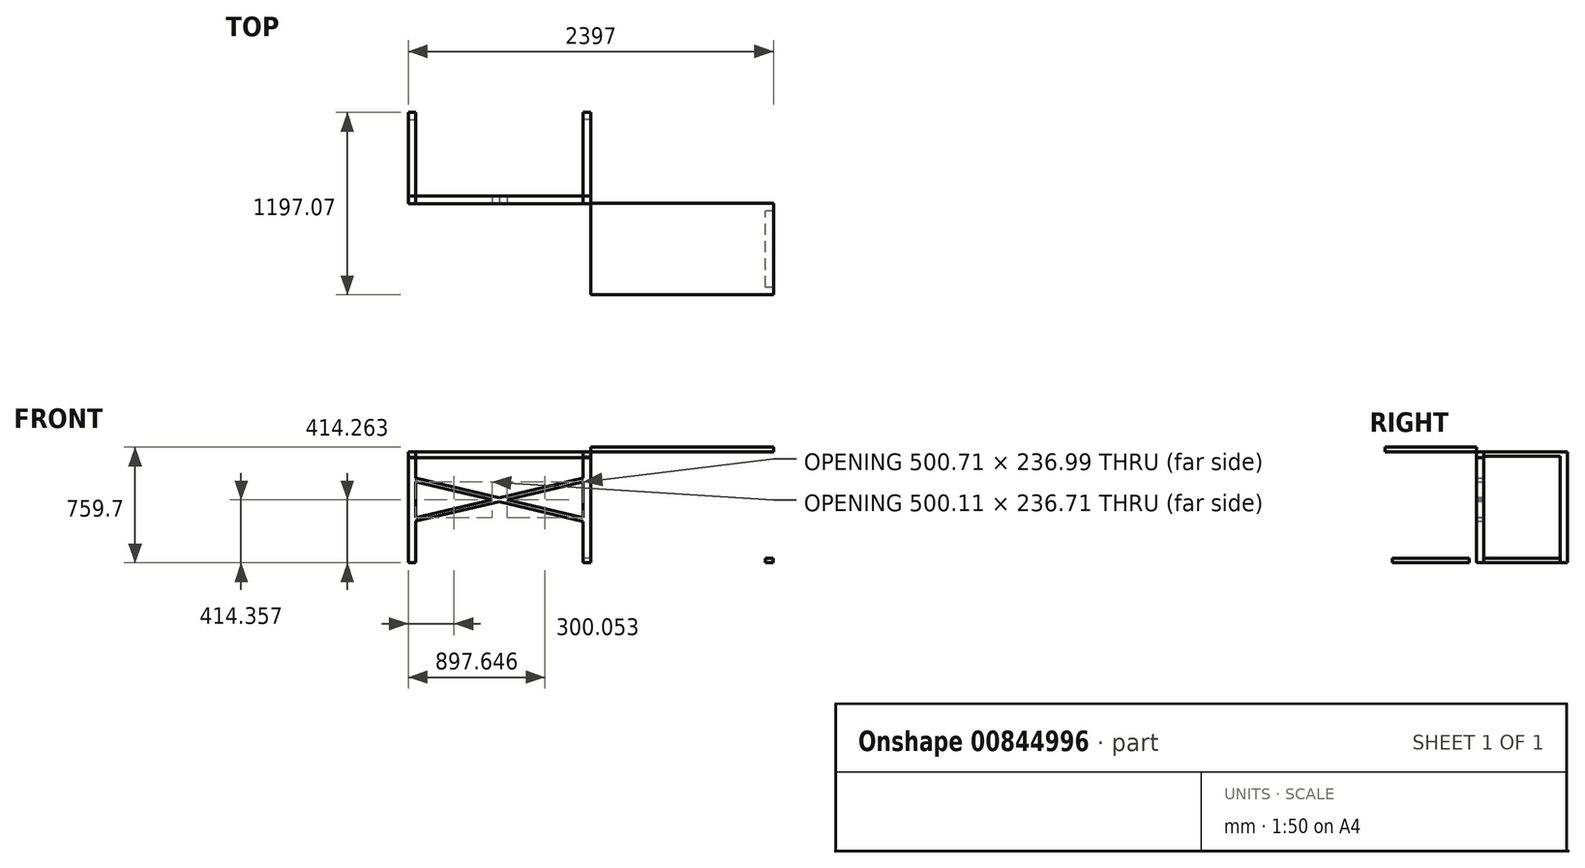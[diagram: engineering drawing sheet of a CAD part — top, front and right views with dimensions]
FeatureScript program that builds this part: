
annotation { "Feature Type Name" : "Feature", "Feature Type Description" : "" }
export const myFeature = defineFeature(function(context is Context, id is Id, definition is map)
    precondition{}
    {
        {
            var Q0;
            Q0=qCreatedBy(makeId("Top.planeOp"),FACE);
            var sketch = newSketch(context, id + "F0", { "sketchPlane" : qUnion([Q0])});
            skLineSegment(sketch, "E0.bottom", {"start": v(600, -300) * mm, "end": v(-600, -300) * mm});
            skLineSegment(sketch, "E0.top", {"start": v(600, 300) * mm, "end": v(-600, 300) * mm});
            skLineSegment(sketch, "E0.left", {"start": v(600, -300) * mm, "end": v(600, 300) * mm});
            skLineSegment(sketch, "E0.right", {"start": v(-600, -300) * mm, "end": v(-600, 300) * mm});
            skPoint(sketch, "E0.middle", {"position": v(0, 0) * mm});
            skSolve(sketch);
        }
        {
            var Q0;
            Q0 = qSketchRegion(id + "F0", true);
            extrude(context, id + "F1", {"entities" : qUnion([Q0]), "depth" : 30 * mm, "offsetDistance" : 25 * mm});
        }
        {
            var Q0;
            Q0=qCreatedBy(makeId("Right.planeOp"),FACE);
            var sketch = newSketch(context, id + "F2", { "sketchPlane" : qUnion([Q0])});
            skLineSegment(sketch, "E1.bottom", {"start": v(-299.02, 0) * mm, "end": v(299.02, 0) * mm});
            skLineSegment(sketch, "E1.top", {"start": v(-299.02, -29.7) * mm, "end": v(299.02, -29.7) * mm});
            skLineSegment(sketch, "E1.left", {"start": v(-299.02, 0) * mm, "end": v(-299.02, -29.7) * mm});
            skLineSegment(sketch, "E1.right", {"start": v(299.02, 0) * mm, "end": v(299.02, -29.7) * mm});
            skSolve(sketch);
        }
        {
            var Q0;
            Q0 = qSketchRegion(id + "F2", true);
            extrude(context, id + "F3", {"entities" : qUnion([Q0]), "depth" : 50 * mm, "offsetDistance" : 25 * mm});
        }
        {
            var Q0;
            Q0=makeQuery(id+"F3.opExtrude","SWEPT_BODY",BODY,{"disambiguationData":[OSD([sQuery(id+"F2.wireOp",EDGE,"E1.bottom"),sQuery(id+"F2.wireOp",EDGE,"E1.top"),sQuery(id+"F2.wireOp",EDGE,"E1.left"),sQuery(id+"F2.wireOp",EDGE,"E1.right")])]});
            transform(context, id + "F4", {"entities" : qUnion([Q0]), "transformType" : TransformType.TRANSLATION_3D, "dx" : 549 * mm, "dy" : 0 * mm, "dz" : 0 * mm, "makeCopy" : false});
        }
        {
            var Q0;
            Q0=makeQuery(id+"F3.opExtrude","SWEPT_BODY",BODY,{"disambiguationData":[OSD([sQuery(id+"F2.wireOp",EDGE,"E1.bottom"),sQuery(id+"F2.wireOp",EDGE,"E1.top"),sQuery(id+"F2.wireOp",EDGE,"E1.left"),sQuery(id+"F2.wireOp",EDGE,"E1.right")])]});
            var Q1;
            Q1=qCreatedBy(makeId("Right.planeOp"),FACE);
            mirror(context, id + "F5", {"entities" : qUnion([Q0]), "mirrorPlane" : qUnion([Q1])});
        }
        {
            var Q0;
            Q0=makeQuery(id+"F5.opPattern","COPY",FACE,{"derivedFrom":makeQuery(id+"F3.opExtrude","SWEPT_FACE",FACE,{"disambiguationData":[OSD([sQuery(id+"F2.wireOp",EDGE,"E1.top")])]}),"instanceName":"1"});
            var sketch = newSketch(context, id + "F6", { "sketchPlane" : qUnion([Q0])});
            skLineSegment(sketch, "E2.bottom", {"start": v(-599, -299.02) * mm, "end": v(-549, -299.02) * mm});
            skLineSegment(sketch, "E2.top", {"start": v(-599, -251.22) * mm, "end": v(-549, -251.22) * mm});
            skLineSegment(sketch, "E2.left", {"start": v(-599, -299.02) * mm, "end": v(-599, -251.22) * mm});
            skLineSegment(sketch, "E2.right", {"start": v(-549, -299.02) * mm, "end": v(-549, -251.22) * mm});
            skSolve(sketch);
        }
        {
            var Q0;
            Q0 = qSketchRegion(id + "F6", true);
            extrude(context, id + "F7", {"entities" : qUnion([Q0]), "depth" : 700 * mm, "offsetDistance" : 25 * mm});
        }
        {
            var Q0;
            Q0=makeQuery(id+"F7.opExtrude","SWEPT_BODY",BODY,{"disambiguationData":[OSD([sQuery(id+"F6.wireOp",EDGE,"E2.bottom"),sQuery(id+"F6.wireOp",EDGE,"E2.top"),sQuery(id+"F6.wireOp",EDGE,"E2.left"),sQuery(id+"F6.wireOp",EDGE,"E2.right")])]});
            var Q1;
            Q1=qCreatedBy(makeId("Right.planeOp"),FACE);
            mirror(context, id + "F8", {"entities" : qUnion([Q0]), "mirrorPlane" : qUnion([Q1])});
        }
        {
            var Q0;
            Q0=makeQuery(id+"F7.opExtrude","SWEPT_BODY",BODY,{"disambiguationData":[OSD([sQuery(id+"F6.wireOp",EDGE,"E2.bottom"),sQuery(id+"F6.wireOp",EDGE,"E2.top"),sQuery(id+"F6.wireOp",EDGE,"E2.left"),sQuery(id+"F6.wireOp",EDGE,"E2.right")])]});
            var Q1;
            Q1=qCreatedBy(makeId("Front.planeOp"),FACE);
            mirror(context, id + "F9", {"operationType" : NewBodyOperationType.ADD, "entities" : qUnion([Q0]), "mirrorPlane" : qUnion([Q1])});
        }
        {
            var Q0;
            Q0=makeQuery(id+"F8.opPattern","COPY",BODY,{"derivedFrom":makeQuery(id+"F7.opExtrude","SWEPT_BODY",BODY,{"disambiguationData":[OSD([sQuery(id+"F6.wireOp",EDGE,"E2.bottom"),sQuery(id+"F6.wireOp",EDGE,"E2.top"),sQuery(id+"F6.wireOp",EDGE,"E2.left"),sQuery(id+"F6.wireOp",EDGE,"E2.right")])]}),"instanceName":"1"});
            var Q1;
            Q1=qCreatedBy(makeId("Front.planeOp"),FACE);
            mirror(context, id + "F10", {"operationType" : NewBodyOperationType.ADD, "entities" : qUnion([Q0]), "mirrorPlane" : qUnion([Q1])});
        }
        {
            var Q0;
            Q0=qCreatedBy(makeId("Top.planeOp"),FACE);
            var sketch = newSketch(context, id + "F11", { "sketchPlane" : qUnion([Q0])});
            skLineSegment(sketch, "E3.bottom", {"start": v(-598.92, -299.03) * mm, "end": v(598.98, -299.03) * mm});
            skLineSegment(sketch, "E3.top", {"start": v(-598.92, -251.27) * mm, "end": v(598.98, -251.27) * mm});
            skLineSegment(sketch, "E3.left", {"start": v(-598.92, -299.03) * mm, "end": v(-598.92, -251.27) * mm});
            skLineSegment(sketch, "E3.right", {"start": v(598.98, -299.03) * mm, "end": v(598.98, -251.27) * mm});
            skSolve(sketch);
        }
        {
            var Q0;
            Q0 = qSketchRegion(id + "F11", true);
            extrude(context, id + "F12", {"entities" : qUnion([Q0]), "oppositeDirection" : true, "depth" : 40 * mm, "offsetDistance" : 25 * mm});
        }
        {
            var Q0;
            Q0=makeQuery(id+"F9.opPattern","COPY",FACE,{"derivedFrom":makeQuery(id+"F7.opExtrude","SWEPT_FACE",FACE,{"disambiguationData":[OSD([sQuery(id+"F6.wireOp",EDGE,"E2.top")])]}),"instanceName":"1"});
            var sketch = newSketch(context, id + "F13", { "sketchPlane" : qUnion([Q0])});
            skLineSegment(sketch, "E4.bottom", {"start": v(599, -729.7) * mm, "end": v(549, -729.7) * mm});
            skLineSegment(sketch, "E4.top", {"start": v(599, -699.7) * mm, "end": v(549, -699.7) * mm});
            skLineSegment(sketch, "E4.left", {"start": v(599, -729.7) * mm, "end": v(599, -699.7) * mm});
            skLineSegment(sketch, "E4.right", {"start": v(549, -729.7) * mm, "end": v(549, -699.7) * mm});
            skLineSegment(sketch, "E5.MirrorCS", {"start": v(-599, -729.7) * mm, "end": v(-599, -699.7) * mm});
            skLineSegment(sketch, "E6.MirrorCS", {"start": v(-599, -729.7) * mm, "end": v(-549, -729.7) * mm});
            skLineSegment(sketch, "E7.MirrorCS", {"start": v(-599, -699.7) * mm, "end": v(-549, -699.7) * mm});
            skLineSegment(sketch, "E8.MirrorCS", {"start": v(-549, -729.7) * mm, "end": v(-549, -699.7) * mm});
            skSolve(sketch);
        }
        {
            var Q0;
            Q0 = qSketchRegion(id + "F13", true);
            extrude(context, id + "F14", {"entities" : qUnion([Q0]), "depth" : 502.5 * mm, "offsetDistance" : 25 * mm});
        }
        {
            var Q0;
            {var subQ0=makeQuery(id+"F7.opExtrude","SWEPT_FACE",FACE,{"disambiguationData":[OSD([sQuery(id+"F6.wireOp",EDGE,"E2.right")])]});Q0=makeQuery(id+"F9.boolean.opBoolean","MERGE",FACE,{"derivedFrom":[makeQuery(id+"F5.opPattern","COPY",FACE,{"derivedFrom":makeQuery(id+"F3.opExtrude","CAP_FACE",FACE,{"disambiguationData":[OSD([sQuery(id+"F2.wireOp",EDGE,"E1.bottom"),sQuery(id+"F2.wireOp",EDGE,"E1.top"),sQuery(id+"F2.wireOp",EDGE,"E1.left"),sQuery(id+"F2.wireOp",EDGE,"E1.right")])],"isStart":true}),"instanceName":"1"}),subQ0,makeQuery(id+"F9.opPattern","COPY",FACE,{"derivedFrom":subQ0,"instanceName":"1"})]});}
            var sketch = newSketch(context, id + "F15", { "sketchPlane" : qUnion([Q0])});
            skLineSegment(sketch, "E9.bottom", {"start": v(-299.02, -174.08) * mm, "end": v(-251.22, -174.08) * mm});
            skLineSegment(sketch, "E9.top", {"start": v(-299.02, -197.08) * mm, "end": v(-251.22, -197.08) * mm});
            skLineSegment(sketch, "E9.left", {"start": v(-299.02, -174.08) * mm, "end": v(-299.02, -197.08) * mm});
            skLineSegment(sketch, "E9.right", {"start": v(-251.22, -174.08) * mm, "end": v(-251.22, -197.08) * mm});
            skSolve(sketch);
        }
        {
            var Q0;
            {var subQ0=makeQuery(id+"F8.opPattern","COPY",FACE,{"derivedFrom":makeQuery(id+"F7.opExtrude","SWEPT_FACE",FACE,{"disambiguationData":[OSD([sQuery(id+"F6.wireOp",EDGE,"E2.right")])]}),"instanceName":"1"});Q0=makeQuery(id+"F10.boolean.opBoolean","MERGE",FACE,{"derivedFrom":[makeQuery(id+"F3.opExtrude","CAP_FACE",FACE,{"disambiguationData":[OSD([sQuery(id+"F2.wireOp",EDGE,"E1.bottom"),sQuery(id+"F2.wireOp",EDGE,"E1.top"),sQuery(id+"F2.wireOp",EDGE,"E1.left"),sQuery(id+"F2.wireOp",EDGE,"E1.right")])],"isStart":true}),subQ0,makeQuery(id+"F10.opPattern","COPY",FACE,{"derivedFrom":subQ0,"instanceName":"1"})]});}
            var sketch = newSketch(context, id + "F16", { "sketchPlane" : qUnion([Q0])});
            skLineSegment(sketch, "E10.bottom", {"start": v(251.22, -433.84) * mm, "end": v(299.02, -433.84) * mm});
            skLineSegment(sketch, "E10.top", {"start": v(251.22, -456.84) * mm, "end": v(299.02, -456.84) * mm});
            skLineSegment(sketch, "E10.left", {"start": v(251.22, -433.84) * mm, "end": v(251.22, -456.84) * mm});
            skLineSegment(sketch, "E10.right", {"start": v(299.02, -433.84) * mm, "end": v(299.02, -456.84) * mm});
            skSolve(sketch);
        }
        {
            var Q2;
            Q2=makeQuery(id+"F15.imprint","IMPRINT",FACE,{"disambiguationData":[TD([[makeQuery(id+"F15.imprint","IMPRINT",EDGE,{"derivedFrom":sQuery(id+"F15.wireOp",EDGE,"E9.bottom")}),-1.0]])]});
            var Q3;
            Q3=makeQuery(id+"F16.imprint","IMPRINT",FACE,{"disambiguationData":[TD([[makeQuery(id+"F16.imprint","IMPRINT",EDGE,{"derivedFrom":sQuery(id+"F16.wireOp",EDGE,"E10.bottom")}),-1.0]])]});
            loft(context, id + "F17", {"operationType" : NewBodyOperationType.ADD, "sheetProfilesArray" : [{ "sheetProfileEntities" : qUnion([Q2]) }, { "sheetProfileEntities" : qUnion([Q3]) }]});
        }
        {
            var Q0;
            {var subQ0=sQuery(id+"F6.wireOp",EDGE,"E2.top");var subQ9=sQuery(id+"F6.wireOp",EDGE,"E2.right");var subQ10=sQuery(id+"F2.wireOp",EDGE,"E1.top");var subQ12=sQuery(id+"F6.wireOp",EDGE,"E2.bottom");var subQ17=sQuery(id+"F2.wireOp",EDGE,"E1.left");var subQ22=makeQuery(id+"F8.opPattern","COPY",FACE,{"derivedFrom":makeQuery(id+"F7.opExtrude","CAP_FACE",FACE,{"disambiguationData":[OSD([subQ12,subQ0,sQuery(id+"F6.wireOp",EDGE,"E2.left"),subQ9])],"isStart":false}),"instanceName":"1"});var subQ26=makeQuery(id+"F8.opPattern","COPY",FACE,{"derivedFrom":makeQuery(id+"F7.opExtrude","SWEPT_FACE",FACE,{"disambiguationData":[OSD([subQ9])]}),"instanceName":"1"});var subQ27=sQuery(id+"F2.wireOp",EDGE,"E1.right");var subQ28=sQuery(id+"F2.wireOp",EDGE,"E1.bottom");var subQ29=makeQuery(id+"F10.boolean.opBoolean","MERGE",FACE,{"derivedFrom":[makeQuery(id+"F3.opExtrude","CAP_FACE",FACE,{"disambiguationData":[OSD([subQ28,subQ10,subQ17,subQ27])],"isStart":true}),subQ26,makeQuery(id+"F10.opPattern","COPY",FACE,{"derivedFrom":subQ26,"instanceName":"1"})]});Q0=makeQuery(id+"FEgc4e0kRUvku2v_5.opBoolean","MERGE",FACE,{"derivedFrom":[makeQuery(id+"F14.opExtrude","SWEPT_FACE",FACE,{"disambiguationData":[OSD([sQuery(id+"F13.wireOp",EDGE,"E8.MirrorCS")])]}),makeQuery(id+"F17.boolean.opBoolean","SPLIT",FACE,{"disambiguationData":[TD([makeQuery(id+"F3.opExtrude","SWEPT_FACE",FACE,{"disambiguationData":[OSD([subQ28])]})])],"derivedFrom":subQ29}),makeQuery(id+"F17.boolean.opBoolean","SPLIT",FACE,{"disambiguationData":[TD([makeQuery(id+"F10.opPattern","COPY",FACE,{"derivedFrom":subQ22,"instanceName":"1"})])],"derivedFrom":subQ29})]});}
            var sketch = newSketch(context, id + "F18", { "sketchPlane" : qUnion([Q0])});
            skLineSegment(sketch, "E11.bottom", {"start": v(299.02, -173.85) * mm, "end": v(251.22, -173.85) * mm});
            skLineSegment(sketch, "E11.top", {"start": v(299.02, -196.85) * mm, "end": v(251.22, -196.85) * mm});
            skLineSegment(sketch, "E11.left", {"start": v(299.02, -173.85) * mm, "end": v(299.02, -196.85) * mm});
            skLineSegment(sketch, "E11.right", {"start": v(251.22, -173.85) * mm, "end": v(251.22, -196.85) * mm});
            skSolve(sketch);
        }
        {
            var Q0;
            {var subQ0=sQuery(id+"F6.wireOp",EDGE,"E2.bottom");var subQ3=sQuery(id+"F6.wireOp",EDGE,"E2.top");var subQ6=sQuery(id+"F2.wireOp",EDGE,"E1.left");var subQ9=sQuery(id+"F6.wireOp",EDGE,"E2.right");var subQ10=makeQuery(id+"F7.opExtrude","CAP_FACE",FACE,{"disambiguationData":[OSD([subQ0,subQ3,sQuery(id+"F6.wireOp",EDGE,"E2.left"),subQ9])],"isStart":false});var subQ21=sQuery(id+"F2.wireOp",EDGE,"E1.top");var subQ24=makeQuery(id+"F7.opExtrude","SWEPT_FACE",FACE,{"disambiguationData":[OSD([subQ9])]});var subQ25=sQuery(id+"F2.wireOp",EDGE,"E1.right");var subQ26=sQuery(id+"F2.wireOp",EDGE,"E1.bottom");var subQ27=makeQuery(id+"F9.boolean.opBoolean","MERGE",FACE,{"derivedFrom":[makeQuery(id+"F5.opPattern","COPY",FACE,{"derivedFrom":makeQuery(id+"F3.opExtrude","CAP_FACE",FACE,{"disambiguationData":[OSD([subQ26,subQ21,subQ6,subQ25])],"isStart":true}),"instanceName":"1"}),subQ24,makeQuery(id+"F9.opPattern","COPY",FACE,{"derivedFrom":subQ24,"instanceName":"1"})]});Q0=makeQuery(id+"FEgc4e0kRUvku2v_5.opBoolean","MERGE",FACE,{"derivedFrom":[makeQuery(id+"F14.opExtrude","SWEPT_FACE",FACE,{"disambiguationData":[OSD([sQuery(id+"F13.wireOp",EDGE,"E4.right")])]}),makeQuery(id+"F17.boolean.opBoolean","SPLIT",FACE,{"disambiguationData":[TD([makeQuery(id+"F5.opPattern","COPY",FACE,{"derivedFrom":makeQuery(id+"F3.opExtrude","SWEPT_FACE",FACE,{"disambiguationData":[OSD([subQ26])]}),"instanceName":"1"})])],"derivedFrom":subQ27}),makeQuery(id+"F17.boolean.opBoolean","SPLIT",FACE,{"disambiguationData":[TD([makeQuery(id+"F9.opPattern","COPY",FACE,{"derivedFrom":subQ10,"instanceName":"1"})])],"derivedFrom":subQ27})]});}
            var sketch = newSketch(context, id + "F19", { "sketchPlane" : qUnion([Q0])});
            skLineSegment(sketch, "E12.bottom", {"start": v(-299.02, -433.8) * mm, "end": v(-251.22, -433.8) * mm});
            skLineSegment(sketch, "E12.top", {"start": v(-299.02, -456.8) * mm, "end": v(-251.22, -456.8) * mm});
            skLineSegment(sketch, "E12.left", {"start": v(-299.02, -433.8) * mm, "end": v(-299.02, -456.8) * mm});
            skLineSegment(sketch, "E12.right", {"start": v(-251.22, -433.8) * mm, "end": v(-251.22, -456.8) * mm});
            skSolve(sketch);
        }
        {
            var Q1;
            Q1=makeQuery(id+"F19.imprint","IMPRINT",FACE,{"disambiguationData":[TD([[makeQuery(id+"F19.imprint","IMPRINT",EDGE,{"derivedFrom":sQuery(id+"F19.wireOp",EDGE,"E12.bottom")}),-1.0]])]});
            var Q2;
            Q2=makeQuery(id+"F18.imprint","IMPRINT",FACE,{"disambiguationData":[TD([[makeQuery(id+"F18.imprint","IMPRINT",EDGE,{"derivedFrom":sQuery(id+"F18.wireOp",EDGE,"E11.bottom")}),1.0]])]});
            loft(context, id + "F20", {"operationType" : NewBodyOperationType.ADD, "sheetProfilesArray" : [{ "sheetProfileEntities" : qUnion([Q1]) }, { "sheetProfileEntities" : qUnion([Q2]) }]});
        }
        {
            var Q0;
            Q0=makeQuery(id+"F14.opExtrude","SWEPT_BODY",BODY,{"disambiguationData":[OSD([sQuery(id+"F13.wireOp",EDGE,"E4.bottom"),sQuery(id+"F13.wireOp",EDGE,"E4.top"),sQuery(id+"F13.wireOp",EDGE,"E4.left"),sQuery(id+"F13.wireOp",EDGE,"E4.right")])]});
            var Q1;
            Q1=makeQuery(id+"F1.opExtrude","SWEPT_BODY",BODY,{"disambiguationData":[OSD([sQuery(id+"F0.wireOp",EDGE,"E0.bottom"),sQuery(id+"F0.wireOp",EDGE,"E0.top"),sQuery(id+"F0.wireOp",EDGE,"E0.left"),sQuery(id+"F0.wireOp",EDGE,"E0.right")])]});
            var Q2;
            Q2=makeQuery(id+"F10.boolean.opBoolean","MERGE",EDGE,{"derivedFrom":[makeQuery(id+"F3.opExtrude","CAP_EDGE",EDGE,{"disambiguationData":[OSD([sQuery(id+"F2.wireOp",EDGE,"E1.left")])],"isStart":false}),makeQuery(id+"F10.opPattern","COPY",EDGE,{"derivedFrom":makeQuery(id+"F8.opPattern","COPY",EDGE,{"derivedFrom":makeQuery(id+"F7.opExtrude","SWEPT_EDGE",EDGE,{"disambiguationData":[OSD([sQuery(id+"F6.wireOp",EDGE,"E2.bottom"),sQuery(id+"F6.wireOp",EDGE,"E2.left")])]}),"instanceName":"1"}),"instanceName":"1"})]});
            transform(context, id + "F21", {"entities" : qUnion([Q0, Q1]), "transformType" : TransformType.ROTATION, "transformAxis" : qUnion([Q2]), "angle" : 180 * degree, "makeCopy" : false});
        }
    });
